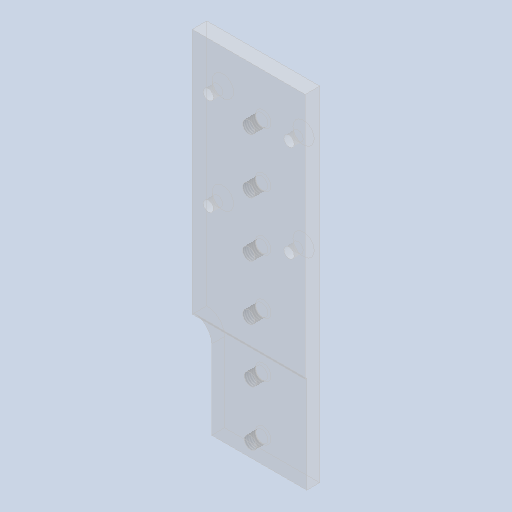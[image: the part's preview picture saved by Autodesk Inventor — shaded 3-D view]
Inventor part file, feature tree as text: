
AUTODESK INVENTOR PART (.ipt)
format: ipt  version: 2022 (Build 260153000, 153)  size: 151,040 bytes
history: native  units: in
note: dims shown in document units (in); Inventor stores cm internally (conversion verified against a paired STEP export)
features: other x4, sketch x2, plane x1
ambient origin geometry x8: Origin, YZ Plane, XZ Plane, XY Plane, X Axis, Y Axis, Z Axis, Center Point
bodies: Solid1 (feature_tree)
feature tree (7):
  other  "Plate.ipt"
  other  "Solid1::Plate.ipt"
  other  "TaggingFeature1"
  sketch  "Sketch1"  dims[d0=0.3937in]
  sketch  "Sketch2"
  plane  "Work Plane1"
  other  "Work Axis1"
